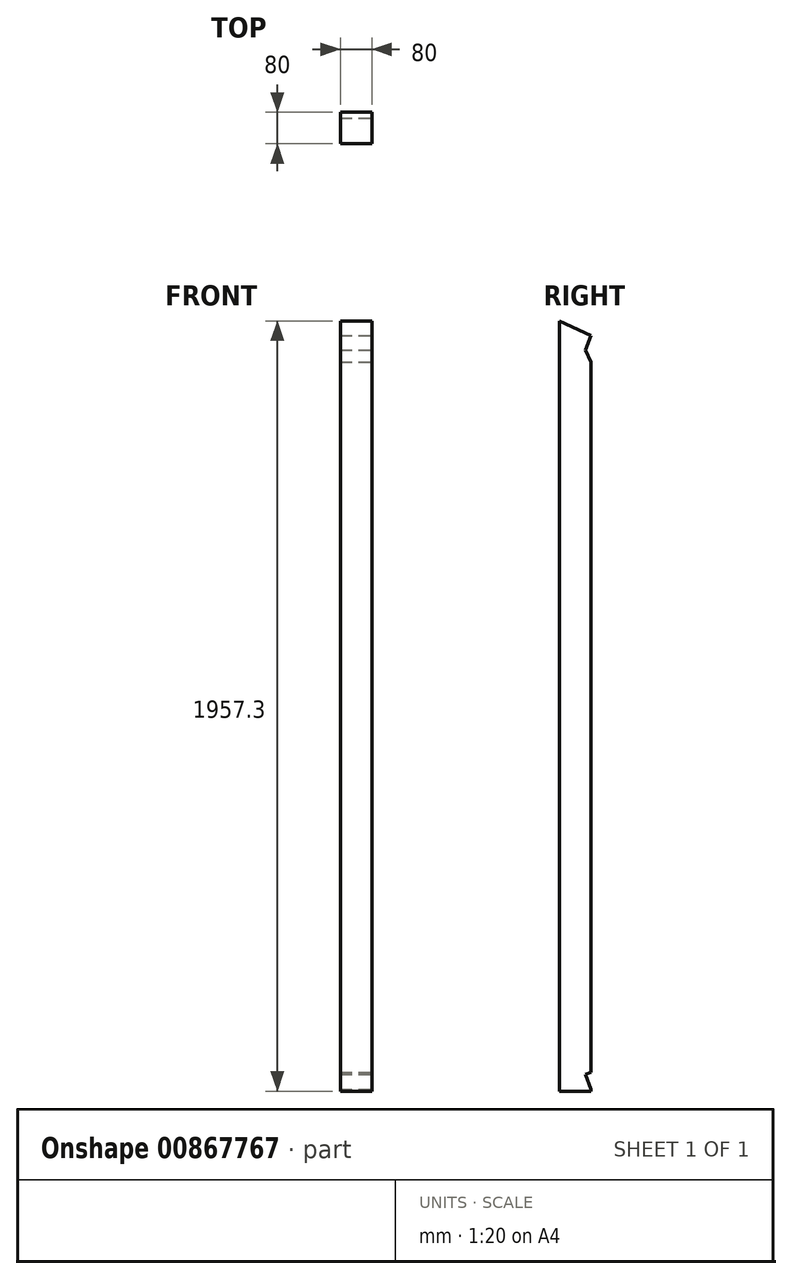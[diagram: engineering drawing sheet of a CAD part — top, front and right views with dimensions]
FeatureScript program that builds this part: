
annotation { "Feature Type Name" : "Feature", "Feature Type Description" : "" }
export const myFeature = defineFeature(function(context is Context, id is Id, definition is map)
    precondition{}
    {
        {
            var Q0;
            Q0=qCreatedBy(makeId("Top.planeOp"),FACE);
            var sketch = newSketch(context, id + "F0", { "sketchPlane" : qUnion([Q0])});
            skLineSegment(sketch, "E0.bottom", {"start": v(40, -40) * mm, "end": v(-40, -40) * mm});
            skLineSegment(sketch, "E0.top", {"start": v(40, 40) * mm, "end": v(-40, 40) * mm});
            skLineSegment(sketch, "E0.left", {"start": v(40, -40) * mm, "end": v(40, 40) * mm});
            skLineSegment(sketch, "E0.right", {"start": v(-40, -40) * mm, "end": v(-40, 40) * mm});
            skPoint(sketch, "E0.middle", {"position": v(0, 0) * mm});
            skSolve(sketch);
        }
        {
            var Q0;
            Q0=makeQuery(id+"F0.imprint","IMPRINT",FACE,{"disambiguationData":[TD([[makeQuery(id+"F0.imprint","IMPRINT",EDGE,{"derivedFrom":sQuery(id+"F0.wireOp",EDGE,"E0.bottom")}),-1.0]])]});
            extrude(context, id + "F1", {"entities" : qUnion([Q0]), "depth" : 2000 * mm, "offsetDistance" : 25 * mm});
        }
        {
            var Q0;
            Q0=makeQuery(id+"F1.opExtrude","SWEPT_FACE",FACE,{"disambiguationData":[OSD([sQuery(id+"F0.wireOp",EDGE,"E0.left")])]});
            var sketch = newSketch(context, id + "F2", { "sketchPlane" : qUnion([Q0])});
            skLineSegment(sketch, "E1.0.0", {"start": v(-40, 0) * mm, "end": v(40, 0) * mm});
            skLineSegment(sketch, "E2.0.1", {"start": v(40, 0) * mm, "end": v(40, 2000) * mm});
            skLineSegment(sketch, "E2.0.2", {"start": v(40, 2000) * mm, "end": v(-40, 2000) * mm});
            skLineSegment(sketch, "E2.0.3", {"start": v(-40, 2000) * mm, "end": v(-40, 0) * mm});
            skLineSegment(sketch, "E3", {"start": v(-40, 1957.3) * mm, "end": v(40, 1920) * mm});
            skLineSegment(sketch, "E4", {"start": v(40, 1920) * mm, "end": v(25.21, 1882.83) * mm});
            skLineSegment(sketch, "E5", {"start": v(25.21, 1882.83) * mm, "end": v(40, 1853.38) * mm});
            skLineSegment(sketch, "E6", {"start": v(25.21, 1882.83) * mm, "end": v(25.21, 42.6) * mm});
            skLineSegment(sketch, "E7", {"start": v(25.21, 42.6) * mm, "end": v(40, 5.43) * mm});
            skLineSegment(sketch, "E8", {"start": v(25.21, 42.6) * mm, "end": v(40, 48.48) * mm});
            skSolve(sketch);
        }
        {
            var Q0;
            {var subQ0=sQuery(id+"F2.wireOp",EDGE,"E4");Q0=makeQuery(id+"F2.imprint","IMPRINT",FACE,{"disambiguationData":[TD([[makeQuery(id+"F2.imprint","IMPRINT",EDGE,{"derivedFrom":subQ0}),1.0]])]});}
            var Q1;
            {var subQ0=sQuery(id+"F2.wireOp",EDGE,"E7");Q1=makeQuery(id+"F2.imprint","IMPRINT",FACE,{"disambiguationData":[TD([[makeQuery(id+"F2.imprint","IMPRINT",EDGE,{"derivedFrom":subQ0}),1.0]])]});}
            var Q2;
            {var subQ0=sQuery(id+"F2.wireOp",EDGE,"E2.0.2");Q2=makeQuery(id+"F2.imprint","IMPRINT",FACE,{"disambiguationData":[TD([[makeQuery(id+"F2.imprint","IMPRINT",EDGE,{"derivedFrom":subQ0}),-1.0]])]});}
            extrude(context, id + "F3", {"entities" : qUnion([Q0, Q1, Q2]), "operationType" : NewBodyOperationType.REMOVE, "endBound" : BoundingType.THROUGH_ALL, "oppositeDirection" : true, "depth" : 25 * mm, "offsetDistance" : 25 * mm});
        }
    });
